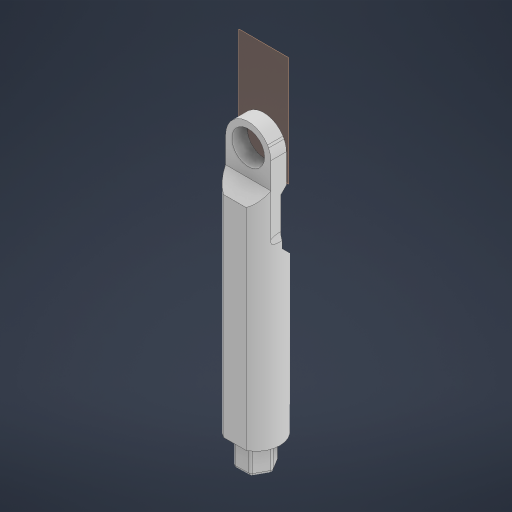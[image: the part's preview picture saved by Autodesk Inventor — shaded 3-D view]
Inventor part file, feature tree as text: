
AUTODESK INVENTOR PART (.ipt)
format: ipt  version: 2024 (Build 280153000, 153)  size: 307,712 bytes
history: native  units: in
note: dims shown in document units (in); Inventor stores cm internally (conversion verified against a paired STEP export)
features: extrude x5, sketch x5, chamfer x4, projected_geometry x4, other x4, fillet x2, reference x2, plane x1
ambient origin geometry x8: Origin, YZ Plane, XZ Plane, XY Plane, X Axis, Y Axis, Z Axis, Center Point
bodies: Solid1 (feature_tree)
feature tree (27):
  plane  "Work Plane1"
  extrude  "Extrusion1"  Depth=5.5118in
  extrude  "Extrusion2"  Depth=1.0236in
  fillet  "Fillet1"  Radius=0.2165in
  extrude  "Extrusion5"  Depth=2.4606in TaperAngle=0.0deg
  fillet  "Fillet3"  Radius=0.25in
  extrude  "Extrusion6"  Depth=0.3937in TaperAngle=0.0deg
  chamfer  "Chamfer2"  Distance=0.4724in
  extrude  "Extrusion7"  Depth=0.0787in TaperAngle=45.0deg
  chamfer  "Chamfer3"  Distance=0.0787in
  chamfer  "Chamfer4"  Distance=0.3543in
  chamfer  "Chamfer5"  Distance=0.2657in Angle=45.0deg
  sketch  "Sketch2"  dims[d1=0.4567in d2=5.5118in]
  reference  "Reference2"
  sketch  "Sketch4"  dims[d3=5.5118in d4=1.0236in d5=0.2165in d6=0.0in]
  reference  "Reference3"
  projected_geometry  "Projected Loop1"
  sketch  "Sketch7"  dims[d7=0.6693in d8=2.4606in d9=0.0in d10=0.25in]
  projected_geometry  "Projected Loop4"
  sketch  "Sketch8"  dims[d24=0.3937in d25=0.3937in d26=0.0in]
  projected_geometry  "Projected Loop5"
  sketch  "Sketch9"  dims[d27=0.0394in d28=0.4724in d29=0.0in d30=0.187in d31=0.125in d32=45.0deg d33=0.0787in d34=0.3543in d35=0.0984in d36=0.0in d37=0.0in d38=0.2657in d39=0.125in d40=45.0deg d41=0.0787in d42=0.125in d43=45.0deg d44=0.1314in d45=0.125in d46=45.0deg]
  projected_geometry  "Projected Loop6"
  other  "<userpath>\Desktop\SeniorDesign\Servo_Shaft.iam"
  other  "Servo_Shaft.iam"
  other  "Servo_Pulley:1"
  other  "Assembly1"
